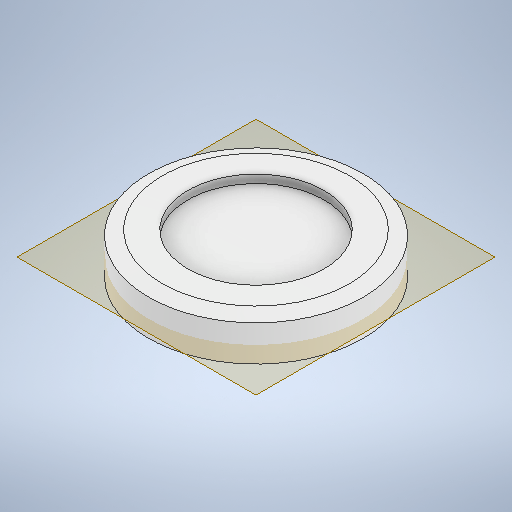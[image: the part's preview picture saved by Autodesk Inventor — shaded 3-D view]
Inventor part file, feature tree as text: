
AUTODESK INVENTOR PART (.ipt)
format: ipt  version: 2025.1 (Build 291241020, 241B)  size: 624,128 bytes
history: native  units: in
note: dims shown in document units (in); Inventor stores cm internally (conversion verified against a paired STEP export)
features: extrude x4, sketch x4, chamfer x2, plane x1, mirror x1
ambient origin geometry x8: Origin, YZ Plane, XZ Plane, XY Plane, X Axis, Y Axis, Z Axis, Center Point
bodies: Solid1 (feature_tree)
feature tree (12):
  extrude  "Extrusion1"  Depth=1.0in
  plane  "Work Plane1"
  extrude  "Extrusion2"  Depth=0.0472in
  extrude  "Extrusion3"  Depth=0.0112in TaperAngle=0.0deg
  extrude  "Extrusion4"  Depth=0.0787in
  chamfer  "Chamfer1"  [1 undecoded]
  chamfer  "Chamfer2"  [1 undecoded]
  sketch  "Sketch1"  dims[d0=1.0in d1=0.0in d2=0.7874in]
  sketch  "Sketch2"  dims[d3=0.0472in d4=0.0in d5=1.2402in]
  sketch  "Sketch3"  dims[d6=0.0in d7=0.0in d8=0.0112in d9=0.0in]
  sketch  "Sketch4"  dims[d10=0.0787in d11=0.0787in d12=0.1374in d13=0.0787in d14=0.0787in d15=0.1374in]
  mirror  "Mirror1"
note: 2 required parameter values undecoded (feature->parameter linkage not recoverable at this tier; creation-order binding heuristic only, values carry confidence <= 0.55)
